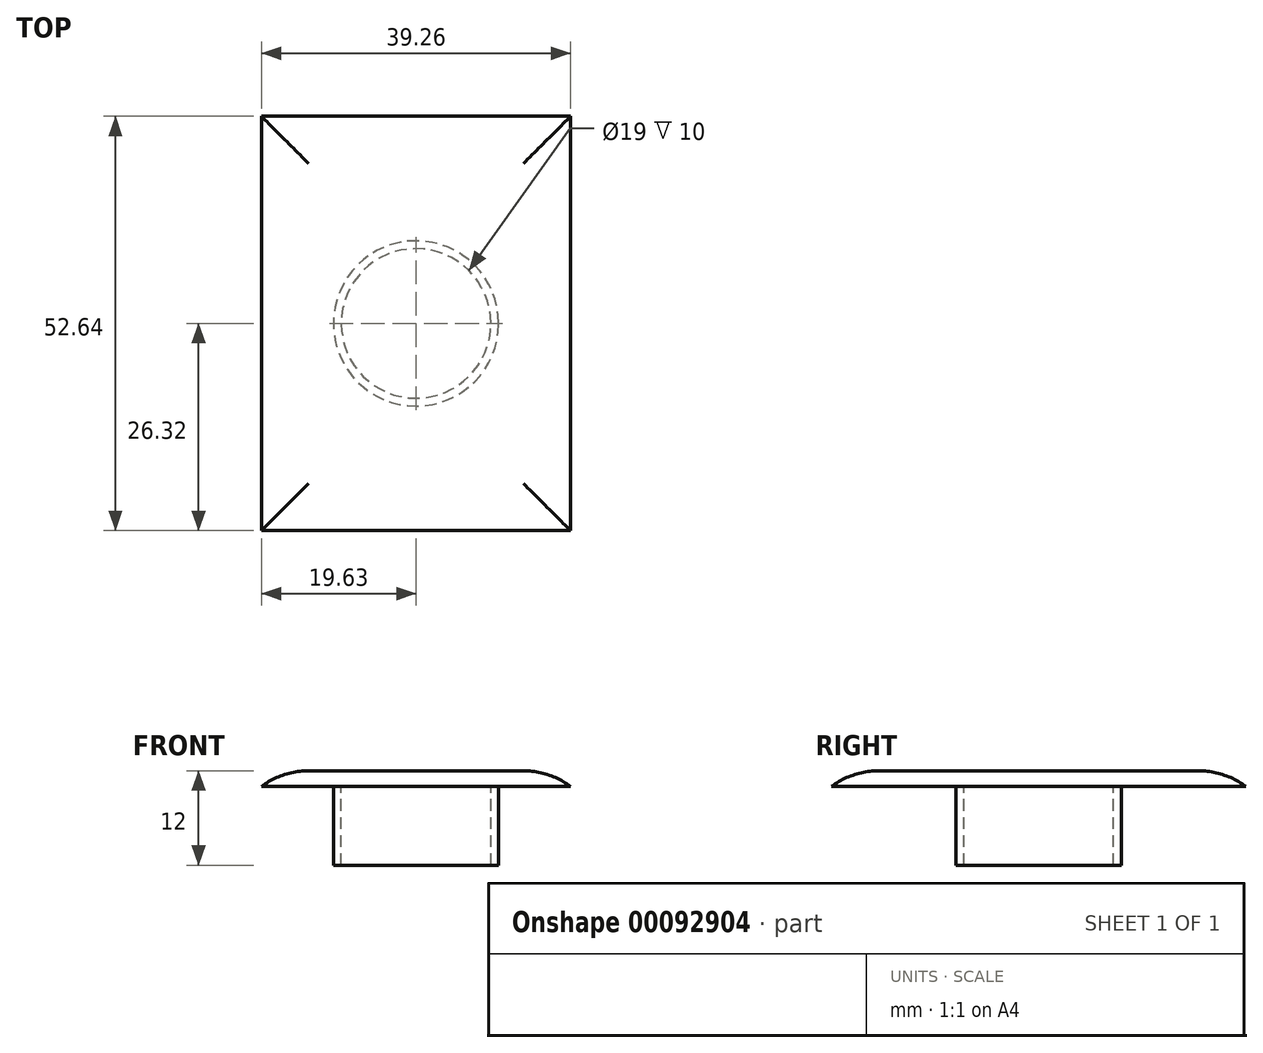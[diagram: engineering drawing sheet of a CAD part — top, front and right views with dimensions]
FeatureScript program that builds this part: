
annotation { "Feature Type Name" : "Feature", "Feature Type Description" : "" }
export const myFeature = defineFeature(function(context is Context, id is Id, definition is map)
    precondition{}
    {
        {
            var Q0;
            Q0=qCreatedBy(makeId("Top.planeOp"),FACE);
            var sketch = newSketch(context, id + "F0", { "sketchPlane" : qUnion([Q0])});
            skCircle(sketch, "E0", {"center": v(0, 0) * mm, "radius": 10.5 * mm});
            skCircle(sketch, "E1", {"center": v(0, 0) * mm, "radius": 9.5 * mm});
            skSolve(sketch);
        }
        {
            var Q0;
            Q0=makeQuery(id+"F0.imprint","IMPRINT",FACE,{"disambiguationData":[TD([[makeQuery(id+"F0.imprint","IMPRINT",EDGE,{"derivedFrom":sQuery(id+"F0.wireOp",EDGE,"E0")}),1.0]])]});
            extrude(context, id + "F1", {"entities" : qUnion([Q0]), "oppositeDirection" : true, "depth" : 10 * mm});
        }
        {
            var Q0;
            Q0=qCreatedBy(makeId("Top.planeOp"),FACE);
            var sketch = newSketch(context, id + "F2", { "sketchPlane" : qUnion([Q0])});
            skLineSegment(sketch, "E2.bottom", {"start": v(19.63, 26.32) * mm, "end": v(-19.63, 26.32) * mm});
            skLineSegment(sketch, "E2.top", {"start": v(19.63, -26.32) * mm, "end": v(-19.63, -26.32) * mm});
            skLineSegment(sketch, "E2.left", {"start": v(19.63, 26.32) * mm, "end": v(19.63, -26.32) * mm});
            skLineSegment(sketch, "E2.right", {"start": v(-19.63, 26.32) * mm, "end": v(-19.63, -26.32) * mm});
            skPoint(sketch, "E2.middle", {"position": v(0, 0) * mm});
            skSolve(sketch);
        }
        {
            var Q0;
            Q0=makeQuery(id+"F2.imprint","IMPRINT",FACE,{"disambiguationData":[TD([[makeQuery(id+"F2.imprint","IMPRINT",EDGE,{"derivedFrom":sQuery(id+"F2.wireOp",EDGE,"E2.bottom")}),1.0]])]});
            var Q1;
            Q1 = qSketchRegion(id + "F2", true);
            extrude(context, id + "F3", {"entities" : qUnion([Q0, Q1]), "operationType" : NewBodyOperationType.ADD, "depth" : 1 * mm});
        }
        {
            var Q0;
            Q0=makeQuery(id+"F3.opExtrude","CAP_FACE",FACE,{"disambiguationData":[OSD([sQuery(id+"F2.wireOp",EDGE,"E2.bottom"),sQuery(id+"F2.wireOp",EDGE,"E2.top"),sQuery(id+"F2.wireOp",EDGE,"E2.left"),sQuery(id+"F2.wireOp",EDGE,"E2.right")])],"isStart":false});
            extrude(context, id + "F4", {"entities" : qUnion([Q0]), "operationType" : NewBodyOperationType.ADD, "depth" : 1 * mm});
        }
        {
            var Q0;
            Q0=makeQuery(id+"F4.opExtrude","CAP_FACE",FACE,{"disambiguationData":[OSD([sQuery(id+"F2.wireOp",EDGE,"E2.bottom"),sQuery(id+"F2.wireOp",EDGE,"E2.top"),sQuery(id+"F2.wireOp",EDGE,"E2.left"),sQuery(id+"F2.wireOp",EDGE,"E2.right")])],"isStart":false});
            fillet(context, id + "F5", {"entities" : qUnion([Q0]), "radius" : 10 * mm, "tangentPropagation" : true, "allowEdgeOverflow" : false});
        }
    });
